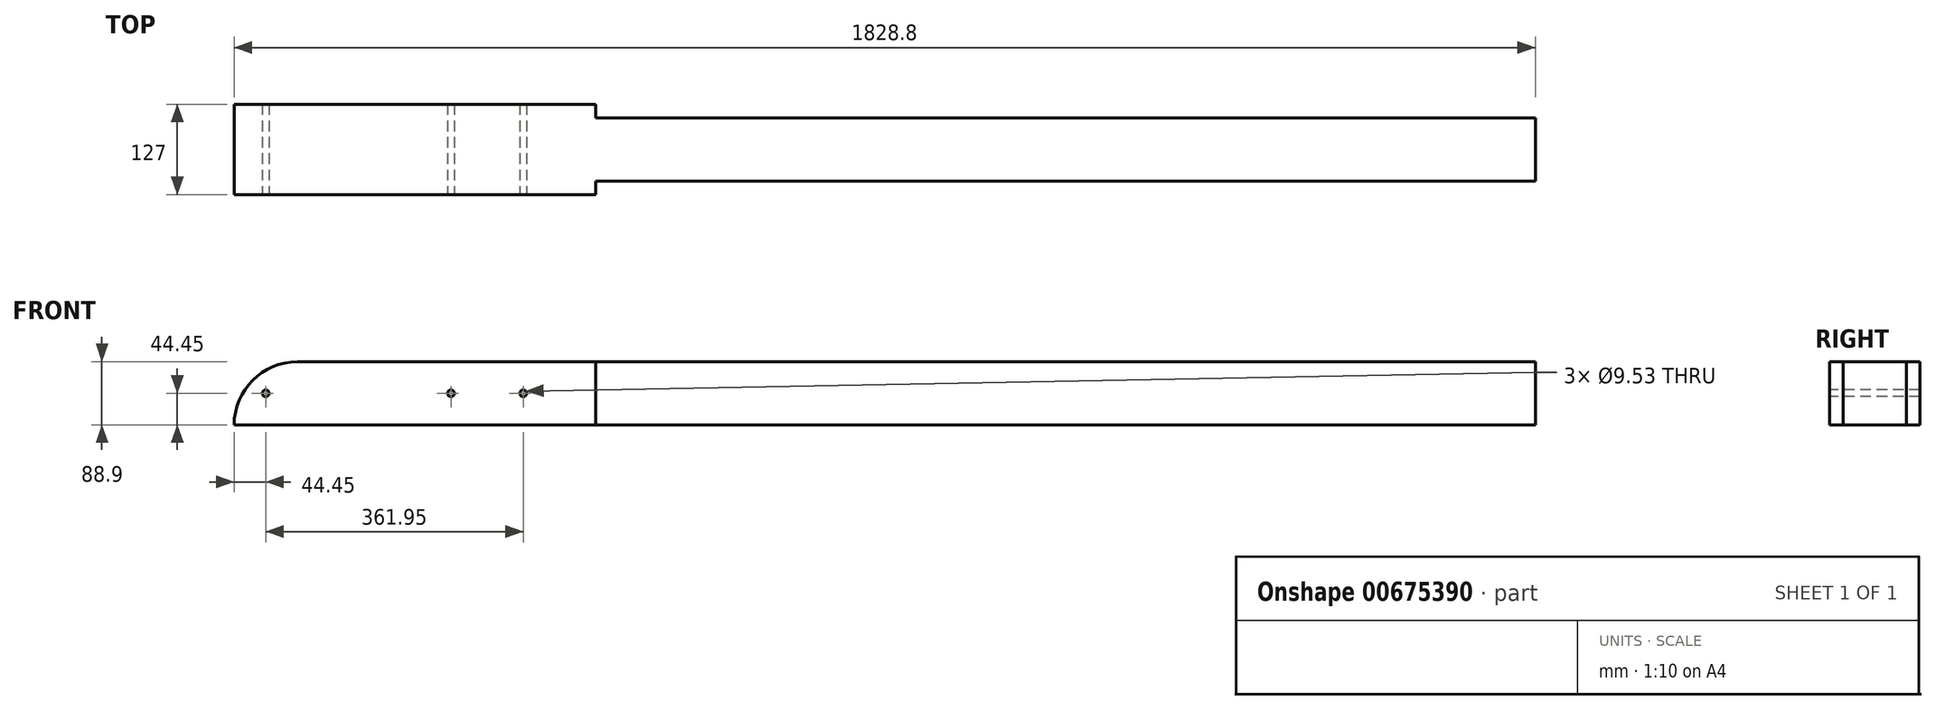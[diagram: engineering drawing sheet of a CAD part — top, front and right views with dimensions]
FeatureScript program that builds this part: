
annotation { "Feature Type Name" : "Feature", "Feature Type Description" : "" }
export const myFeature = defineFeature(function(context is Context, id is Id, definition is map)
    precondition{}
    {
        {
            var Q0;
            Q0=qCreatedBy(makeId("Top.planeOp"),FACE);
            var sketch = newSketch(context, id + "F0", { "sketchPlane" : qUnion([Q0])});
            skLineSegment(sketch, "E0.bottom", {"start": v(508, -44.45) * mm, "end": v(1828.8, -44.45) * mm});
            skLineSegment(sketch, "E0.top", {"start": v(508, 44.45) * mm, "end": v(1828.8, 44.45) * mm});
            skLineSegment(sketch, "E0.left", {"start": v(0, -44.45) * mm, "end": v(0, 44.45) * mm});
            skLineSegment(sketch, "E0.right", {"start": v(1828.8, -44.45) * mm, "end": v(1828.8, 44.45) * mm});
            skLineSegment(sketch, "E1.bottom", {"start": v(0, -63.5) * mm, "end": v(508, -63.5) * mm});
            skLineSegment(sketch, "E1.top", {"start": v(0, 63.5) * mm, "end": v(508, 63.5) * mm});
            skLineSegment(sketch, "E1.left", {"start": v(0, -63.5) * mm, "end": v(0, 63.5) * mm});
            skLineSegment(sketch, "E1.right", {"start": v(508, -63.5) * mm, "end": v(508, -44.45) * mm});
            skLineSegment(sketch, "E2.trimOffspring", {"start": v(508, 44.45) * mm, "end": v(508, 63.5) * mm});
            skSolve(sketch);
        }
        {
            var Q0;
            Q0 = qSketchRegion(id + "F0", true);
            extrude(context, id + "F1", {"entities" : qUnion([Q0]), "depth" : 88.9 * mm, "offsetDistance" : 25.4 * mm});
        }
        {
            var Q0;
            Q0=makeQuery(id+"F1.opExtrude","SWEPT_FACE",FACE,{"disambiguationData":[OSD([sQuery(id+"F0.wireOp",EDGE,"E1.bottom")])]});
            var sketch = newSketch(context, id + "F2", { "sketchPlane" : qUnion([Q0])});
            skCircle(sketch, "E3", {"center": v(44.45, 44.45) * mm, "radius": 4.76 * mm});
            skCircle(sketch, "E4", {"center": v(304.8, 44.45) * mm, "radius": 4.76 * mm});
            skCircle(sketch, "E5", {"center": v(406.4, 44.45) * mm, "radius": 4.76 * mm});
            skSolve(sketch);
        }
        {
            var Q0;
            Q0 = qSketchRegion(id + "F2", true);
            extrude(context, id + "F3", {"entities" : qUnion([Q0]), "operationType" : NewBodyOperationType.REMOVE, "endBound" : BoundingType.THROUGH_ALL, "oppositeDirection" : true, "depth" : 25.4 * mm, "offsetDistance" : 25.4 * mm});
        }
        {
            var Q0;
            Q0=makeQuery(id+"F1.opExtrude","SWEPT_FACE",FACE,{"disambiguationData":[OSD([sQuery(id+"F0.wireOp",EDGE,"E1.bottom")])]});
            var sketch = newSketch(context, id + "F4", { "sketchPlane" : qUnion([Q0])});
            skArc(sketch, "E6", {"start": v(88.9, 88.9) * mm, "mid": v(26.04, 62.86) * mm, "end": v(0, 0) * mm});
            skLineSegment(sketch, "E7", {"start": v(0, 0) * mm, "end": v(0, 88.9) * mm});
            skLineSegment(sketch, "E8", {"start": v(0, 88.9) * mm, "end": v(88.9, 88.9) * mm});
            skSolve(sketch);
        }
        {
            var Q0;
            Q0 = qSketchRegion(id + "F4", true);
            extrude(context, id + "F5", {"entities" : qUnion([Q0]), "operationType" : NewBodyOperationType.REMOVE, "endBound" : BoundingType.THROUGH_ALL, "oppositeDirection" : true, "depth" : 25.4 * mm, "offsetDistance" : 25.4 * mm});
        }
    });
